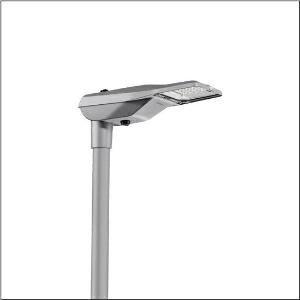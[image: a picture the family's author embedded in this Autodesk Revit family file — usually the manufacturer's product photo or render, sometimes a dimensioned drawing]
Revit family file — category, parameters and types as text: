
# Revit family: streetlight_sl_21_iq_micro___st1_0ab_5xe1m31y08db_79d8
name_source: partatom
category: Lighting Fixtures
units: mm (PartAtom-declared; Revit-internal decimal feet)

## family parameters
Cut with Voids When Loaded = No
Host = Face
Light Source = No
Part Type = Normal
Room Calculation Point = No
Round Connector Dimension = Use Diameter
Shared = No

## types (1)
- --- (1 x LED, 4490 lm, 39.1 W, 3000K)
    Apparent Load = 39 VA
    CIE Flux Codes = 38 73 97 100 100
    Color Rendering = 70
    Color Temperature = 3000K
    Default Elevation = 1800 mm
    Description = Streetlight SL 21 iQ micro, mast luminaire, primary light control with lens, of PMMA, primary optical cover: cover, of toughened safety glass, transparent, light distribution: ST1.0aB, light emission: direct distribution, primary light characteristic: asymmetric, installation type: post-top, side-entry, LED, High Power LED, rated luminous flux: 4.490lm, luminous efficacy: 115lm/W, light colour: 730, colour temperature: 3000K, control: pre-setting: logarithmic dimming characteristic, Street-Remote, Auto-Match, Temp-Guard, Lumen-Switch, Night-Set, Smart-Wire, Light-Fading, Desk-Remote (wireless, voltage-free reading and setting of iQ features in the workshop via application-optimized NFC function/RFID function), optimised constant luminous flux control (CLO 2.0), mains connection: 220..240V, AC, 50/60Hz, start of lifetime: 39W, end of service life: 41W, reduction: 17W, luminaire housing, of diecast aluminium, powder-coated, Siteco® metallic grey (DB 702S), corrosivity category C5 mid according to DIN EN ISO 12944, please order mast flange separately, inclination adjustable: 0°, 5°, 10°, 15°, sealing non-destructively replaceable, multi-level sealing system, length: 528mm, width: 235mm, height: 110mm, mast flange for spigot size: 42mm (side-entry): 5XC10008XM4, 60/48mm (side-entry/post-top): 5XC10108XM2, 76/60mm (side-entry/post-top): 5XC10108XM1, Smart Interface below and above, protection rating (complete): IP66, insulation class (complete): insulation class II (safety insulation), certification: CE, ENEC, ENEC+, VDE, impact resistance: IK09, permissible operating ambient temperature for outdoor applications: -40..+50°C, standard-compliant lighting for roads and squares, packaging unit: 1 piece

Light Distribution: ST1.0aB
    Height = 110 mm
    Lamp = 1 x LED
    Lamp Light Flux = 4490 lm
    Lamp Power = 39.1 W
    Lamp count = 1
    Length = 528 mm
    Luminous efficacy = 115 lm/W
    Manufacturer = Siteco
    ModVariant = No
    Model = 5XE1M31Y08DB
    Number of Poles = 1
    OnlyDefault = Yes
    Power Factor = 1
    Product Name = Streetlight SL 21 iQ micro | ST1.0aB
    Product group = mast luminaire | pylon top
    ProductGroupID = 6100
    Protection Class = Protection class II
    Protection Degree = IP 66
    RLX_Detail_Level = 1
    RLX_Emergency_Light_Flux = 0 lm
    RLX_Emergency_Type = 0
    RLX_Emergency_Type_DB = No
    RlxData = <blob elided: 98333 chars, md5=58f4e376>
    Socket = socket
    Standby Power = 0 W
    System Light Flux = 4490 lm
    System Power = 39 W
    Type Comments = factory setting: luminous flux: 100 % | dim-lin: 254 | 765 mA
    Type Image = l_1007239.jpg
    URL = http://relux.com
    VarID = @adj_081481
    Voltage = 0 V
    Weight = 0.00 kg
    Width = 235 mm

## geometry (parser evidence)
native form markers: Blend x4, Sweep x9
no freeform markers — native parametric forms only
